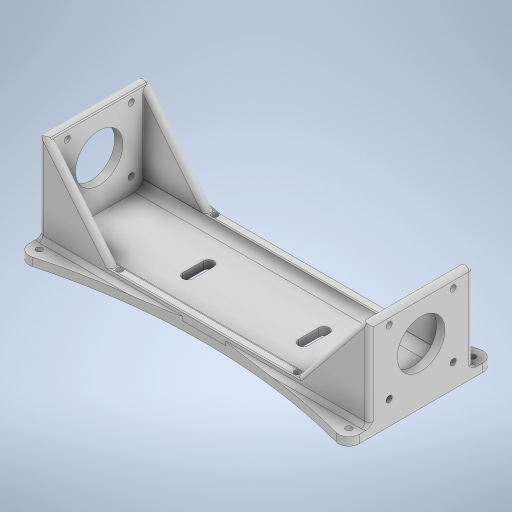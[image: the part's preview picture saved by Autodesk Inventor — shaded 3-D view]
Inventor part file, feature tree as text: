
AUTODESK INVENTOR PART (.ipt)
format: ipt  version: 2023 (Build 270158000, 158)  size: 490,496 bytes
history: native  units: mm
features: sketch x9, extrude x4, hole x4, fillet x4, mirror x3, chamfer x1, projected_geometry x1
ambient origin geometry x8: Origin, YZ Plane, XZ Plane, XY Plane, X Axis, Y Axis, Z Axis, Center Point
bodies: Solid1 (feature_tree)
feature tree (26):
  extrude  "Extrusion1"  Depth=4.0mm TaperAngle=0.0deg
  extrude  "Extrusion3"  Depth=4.0mm
  extrude  "Extrusion4"  Depth=4.0mm
  chamfer  "Chamfer2"  Distance=4.0mm
  mirror  "Mirror2"
  hole  "Hole1"  [1 undecoded]
  hole  "Hole2"  [1 undecoded]
  mirror  "Mirror3"
  extrude  "Extrusion5"  Depth=15.5mm
  mirror  "Mirror4"
  sketch  "Sketch12"  dims[d37=15.5mm d38=15.5mm d39=40.0mm d41=360.0deg]
  fillet  "Fillet10"  Radius=40.0mm
  hole  "Hole3"  [1 undecoded]
  hole  "Hole4"  [1 undecoded]
  fillet  "Fillet13"  Radius=40.0mm
  fillet  "Fillet14"  Radius=60.0mm
  fillet  "Fillet15"  Radius=5.0mm
  sketch  "Sketch1"  dims[d1=160.0mm d2=4.0mm d3=0.0mm]
  sketch  "Sketch2"  dims[d6=50.4mm d7=4.0mm]
  sketch  "Sketch5"  dims[d23=4.0mm d24=4.0mm]
  projected_geometry  "Projected Loop1"
  sketch  "Sketch7"  dims[d25=4.0mm d26=4.0mm d27=0.0mm]
  sketch  "Sketch8"  dims[d28=35.0mm d29=42.0mm d30=0.0mm]
  sketch  "Sketch9"  dims[d31=34.0mm d32=42.0mm d33=45.0deg d36=23.0mm]
  sketch  "Sketch13"  dims[d43=2.9mm d44=6.0mm d45=4.4mm d46=2.0mm d47=90.0deg d48=8.0mm d49=20.594885mm d50=23.0mm]
  sketch  "Sketch14"  dims[d51=23.0mm d52=6.0mm d53=20.0mm d54=2.0mm d55=90.0deg d56=8.0mm d57=20.594885mm d61=10.0mm d63=40.0mm d64=0.0mm d71=60.0mm d73=5.0mm d74=50.0mm d75=2.0mm d76=2.9mm d77=6.0mm d78=5.5mm d79=2.0mm d80=90.0deg d81=8.0mm d82=20.594885mm d85=5.0mm d99=46.0mm d100=86.0mm d101=2.9mm d102=6.0mm d103=4.0mm d104=2.0mm d105=90.0deg d106=8.0mm d107=20.594885mm d109=28.0mm d111=2.0mm d112=4.0mm d113=0.5mm d15=0.0mm d16=0.0mm d17=0.0mm d18=0.0mm d34=0.0mm d35=0.0mm d114=0.0mm]
note: 4 required parameter values undecoded (feature->parameter linkage not recoverable at this tier; creation-order binding heuristic only, values carry confidence <= 0.55)
